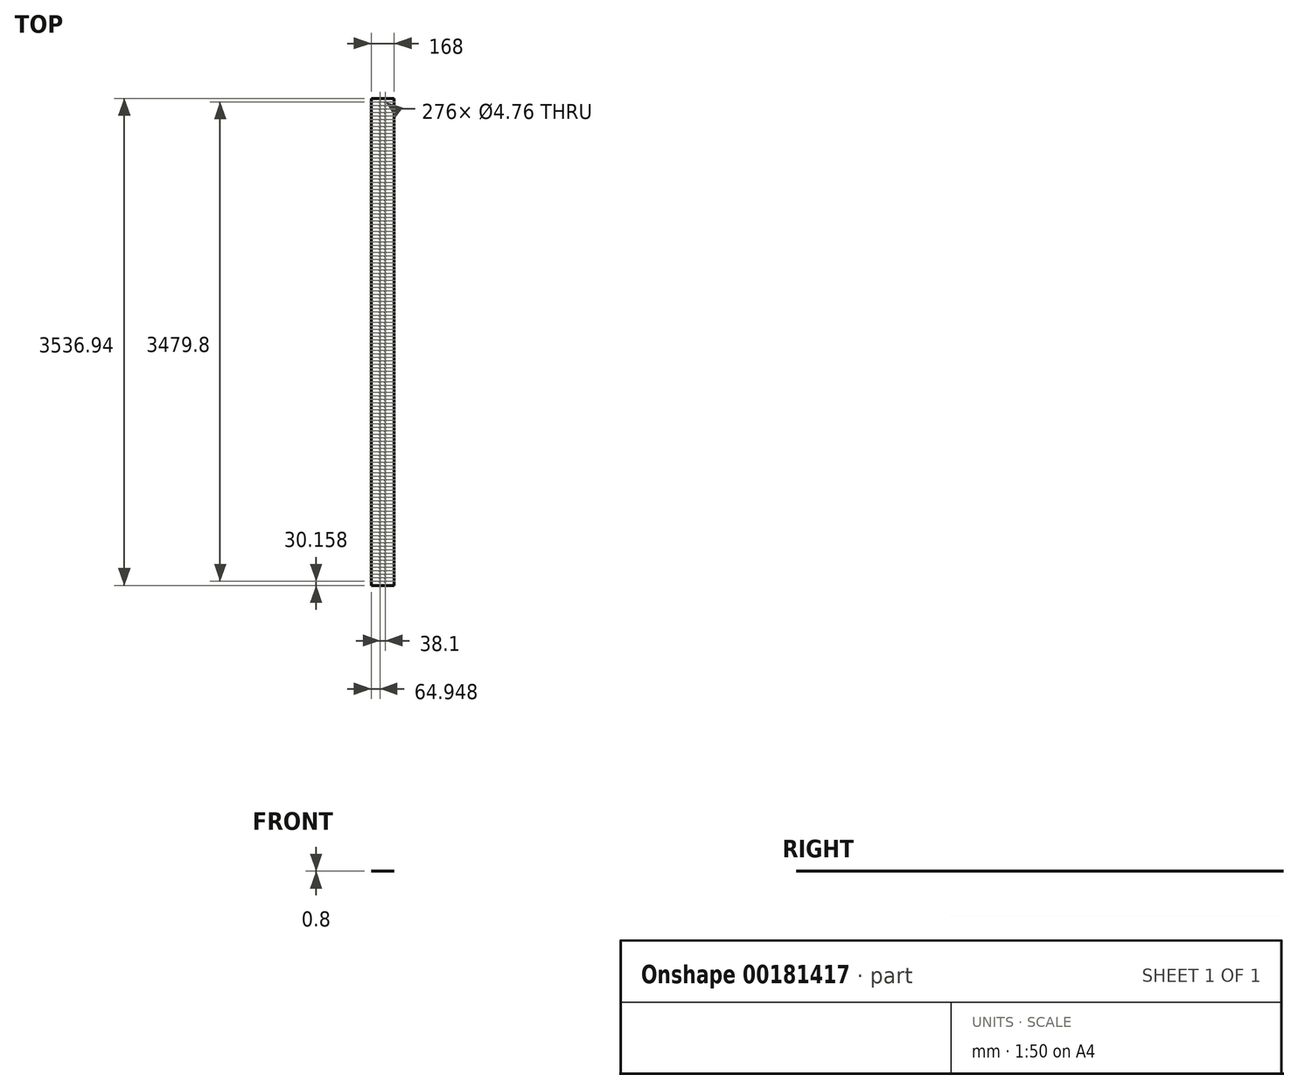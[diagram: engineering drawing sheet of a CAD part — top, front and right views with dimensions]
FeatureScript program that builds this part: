
annotation { "Feature Type Name" : "Feature", "Feature Type Description" : "" }
export const myFeature = defineFeature(function(context is Context, id is Id, definition is map)
    precondition{}
    {
        {
            var Q0;
            Q0=qCreatedBy(makeId("Top.planeOp"),FACE);
            var sketch = newSketch(context, id + "F0", { "sketchPlane" : qUnion([Q0])});
            skLineSegment(sketch, "E0.bottom", {"start": v(84, -1768.48) * mm, "end": v(-84, -1768.48) * mm});
            skLineSegment(sketch, "E0.top", {"start": v(84, 1768.48) * mm, "end": v(-84, 1768.48) * mm});
            skLineSegment(sketch, "E0.left", {"start": v(84, -1768.48) * mm, "end": v(84, 1768.48) * mm});
            skLineSegment(sketch, "E0.right", {"start": v(-84, -1768.48) * mm, "end": v(-84, 1768.48) * mm});
            skPoint(sketch, "E0.middle", {"position": v(0, 0) * mm});
            skCircle(sketch, "E1", {"center": v(-19.05, -1738.31) * mm, "radius": 2.38 * mm});
            skCircle(sketch, "E2.0.1.0", {"center": v(-19.05, -1712.91) * mm, "radius": 2.38 * mm});
            skCircle(sketch, "E2.0.2.0", {"center": v(-19.05, -1687.51) * mm, "radius": 2.38 * mm});
            skCircle(sketch, "E2.0.3.0", {"center": v(-19.05, -1662.11) * mm, "radius": 2.38 * mm});
            skCircle(sketch, "E2.0.4.0", {"center": v(-19.05, -1636.71) * mm, "radius": 2.38 * mm});
            skCircle(sketch, "E2.0.5.0", {"center": v(-19.05, -1611.31) * mm, "radius": 2.38 * mm});
            skCircle(sketch, "E2.0.6.0", {"center": v(-19.05, -1585.91) * mm, "radius": 2.38 * mm});
            skCircle(sketch, "E2.0.7.0", {"center": v(-19.05, -1560.51) * mm, "radius": 2.38 * mm});
            skCircle(sketch, "E2.0.8.0", {"center": v(-19.05, -1535.11) * mm, "radius": 2.38 * mm});
            skCircle(sketch, "E2.0.9.0", {"center": v(-19.05, -1509.71) * mm, "radius": 2.38 * mm});
            skCircle(sketch, "E2.0.10.0", {"center": v(-19.05, -1484.31) * mm, "radius": 2.38 * mm});
            skCircle(sketch, "E2.0.11.0", {"center": v(-19.05, -1458.91) * mm, "radius": 2.38 * mm});
            skCircle(sketch, "E2.0.12.0", {"center": v(-19.05, -1433.51) * mm, "radius": 2.38 * mm});
            skCircle(sketch, "E2.0.13.0", {"center": v(-19.05, -1408.11) * mm, "radius": 2.38 * mm});
            skCircle(sketch, "E2.0.14.0", {"center": v(-19.05, -1382.71) * mm, "radius": 2.38 * mm});
            skLineSegment(sketch, "E2.direction1", {"start": v(-19.05, -1738.31) * mm, "end": v(19.05, -1738.31) * mm, "construction": true});
            skLineSegment(sketch, "E2.direction2", {"start": v(-19.05, -1738.31) * mm, "end": v(-19.05, -1712.91) * mm, "construction": true});
            skCircle(sketch, "E3.0.1.0", {"center": v(19.05, -1738.31) * mm, "radius": 2.38 * mm});
            skCircle(sketch, "E3.0.1.1", {"center": v(19.05, -1712.91) * mm, "radius": 2.38 * mm});
            skCircle(sketch, "E3.0.1.2", {"center": v(19.05, -1687.51) * mm, "radius": 2.38 * mm});
            skCircle(sketch, "E3.0.1.3", {"center": v(19.05, -1662.11) * mm, "radius": 2.38 * mm});
            skCircle(sketch, "E3.0.1.4", {"center": v(19.05, -1636.71) * mm, "radius": 2.38 * mm});
            skCircle(sketch, "E3.0.1.5", {"center": v(19.05, -1611.31) * mm, "radius": 2.38 * mm});
            skCircle(sketch, "E3.0.1.6", {"center": v(19.05, -1585.91) * mm, "radius": 2.38 * mm});
            skCircle(sketch, "E3.0.1.7", {"center": v(19.05, -1560.51) * mm, "radius": 2.38 * mm});
            skCircle(sketch, "E3.0.1.8", {"center": v(19.05, -1535.11) * mm, "radius": 2.38 * mm});
            skCircle(sketch, "E3.0.1.9", {"center": v(19.05, -1509.71) * mm, "radius": 2.38 * mm});
            skCircle(sketch, "E3.0.1.10", {"center": v(19.05, -1484.31) * mm, "radius": 2.38 * mm});
            skCircle(sketch, "E3.0.1.11", {"center": v(19.05, -1458.91) * mm, "radius": 2.38 * mm});
            skCircle(sketch, "E3.0.1.12", {"center": v(19.05, -1433.51) * mm, "radius": 2.38 * mm});
            skCircle(sketch, "E3.0.1.13", {"center": v(19.05, -1408.11) * mm, "radius": 2.38 * mm});
            skCircle(sketch, "E3.0.1.14", {"center": v(19.05, -1382.71) * mm, "radius": 2.38 * mm});
            skCircle(sketch, "E4.0.0.15", {"center": v(-19.05, -1357.31) * mm, "radius": 2.38 * mm});
            skCircle(sketch, "E4.0.0.16", {"center": v(-19.05, -1331.91) * mm, "radius": 2.38 * mm});
            skCircle(sketch, "E4.0.0.17", {"center": v(-19.05, -1306.51) * mm, "radius": 2.38 * mm});
            skCircle(sketch, "E4.0.0.18", {"center": v(-19.05, -1281.11) * mm, "radius": 2.38 * mm});
            skCircle(sketch, "E4.0.0.19", {"center": v(-19.05, -1255.71) * mm, "radius": 2.38 * mm});
            skCircle(sketch, "E4.0.0.20", {"center": v(-19.05, -1230.31) * mm, "radius": 2.38 * mm});
            skCircle(sketch, "E4.0.0.21", {"center": v(-19.05, -1204.91) * mm, "radius": 2.38 * mm});
            skCircle(sketch, "E4.0.0.22", {"center": v(-19.05, -1179.51) * mm, "radius": 2.38 * mm});
            skCircle(sketch, "E4.0.0.23", {"center": v(-19.05, -1154.11) * mm, "radius": 2.38 * mm});
            skCircle(sketch, "E4.0.0.24", {"center": v(-19.05, -1128.71) * mm, "radius": 2.38 * mm});
            skCircle(sketch, "E4.0.0.25", {"center": v(-19.05, -1103.31) * mm, "radius": 2.38 * mm});
            skCircle(sketch, "E4.0.0.26", {"center": v(-19.05, -1077.91) * mm, "radius": 2.38 * mm});
            skCircle(sketch, "E4.0.0.27", {"center": v(-19.05, -1052.51) * mm, "radius": 2.38 * mm});
            skCircle(sketch, "E4.0.0.28", {"center": v(-19.05, -1027.11) * mm, "radius": 2.38 * mm});
            skCircle(sketch, "E4.0.0.29", {"center": v(-19.05, -1001.71) * mm, "radius": 2.38 * mm});
            skCircle(sketch, "E4.0.1.15", {"center": v(19.05, -1357.31) * mm, "radius": 2.38 * mm});
            skCircle(sketch, "E4.0.1.16", {"center": v(19.05, -1331.91) * mm, "radius": 2.38 * mm});
            skCircle(sketch, "E4.0.1.17", {"center": v(19.05, -1306.51) * mm, "radius": 2.38 * mm});
            skCircle(sketch, "E4.0.1.18", {"center": v(19.05, -1281.11) * mm, "radius": 2.38 * mm});
            skCircle(sketch, "E4.0.1.19", {"center": v(19.05, -1255.71) * mm, "radius": 2.38 * mm});
            skCircle(sketch, "E4.0.1.20", {"center": v(19.05, -1230.31) * mm, "radius": 2.38 * mm});
            skCircle(sketch, "E4.0.1.21", {"center": v(19.05, -1204.91) * mm, "radius": 2.38 * mm});
            skCircle(sketch, "E4.0.1.22", {"center": v(19.05, -1179.51) * mm, "radius": 2.38 * mm});
            skCircle(sketch, "E4.0.1.23", {"center": v(19.05, -1154.11) * mm, "radius": 2.38 * mm});
            skCircle(sketch, "E4.0.1.24", {"center": v(19.05, -1128.71) * mm, "radius": 2.38 * mm});
            skCircle(sketch, "E4.0.1.25", {"center": v(19.05, -1103.31) * mm, "radius": 2.38 * mm});
            skCircle(sketch, "E4.0.1.26", {"center": v(19.05, -1077.91) * mm, "radius": 2.38 * mm});
            skCircle(sketch, "E4.0.1.27", {"center": v(19.05, -1052.51) * mm, "radius": 2.38 * mm});
            skCircle(sketch, "E4.0.1.28", {"center": v(19.05, -1027.11) * mm, "radius": 2.38 * mm});
            skCircle(sketch, "E4.0.1.29", {"center": v(19.05, -1001.71) * mm, "radius": 2.38 * mm});
            skCircle(sketch, "E5.0.0.30", {"center": v(-19.05, -976.31) * mm, "radius": 2.38 * mm});
            skCircle(sketch, "E5.0.0.31", {"center": v(-19.05, -950.91) * mm, "radius": 2.38 * mm});
            skCircle(sketch, "E5.0.0.32", {"center": v(-19.05, -925.51) * mm, "radius": 2.38 * mm});
            skCircle(sketch, "E5.0.0.33", {"center": v(-19.05, -900.11) * mm, "radius": 2.38 * mm});
            skCircle(sketch, "E5.0.0.34", {"center": v(-19.05, -874.71) * mm, "radius": 2.38 * mm});
            skCircle(sketch, "E5.0.0.35", {"center": v(-19.05, -849.31) * mm, "radius": 2.38 * mm});
            skCircle(sketch, "E5.0.0.36", {"center": v(-19.05, -823.91) * mm, "radius": 2.38 * mm});
            skCircle(sketch, "E5.0.0.37", {"center": v(-19.05, -798.51) * mm, "radius": 2.38 * mm});
            skCircle(sketch, "E5.0.0.38", {"center": v(-19.05, -773.11) * mm, "radius": 2.38 * mm});
            skCircle(sketch, "E5.0.0.39", {"center": v(-19.05, -747.71) * mm, "radius": 2.38 * mm});
            skCircle(sketch, "E5.0.0.40", {"center": v(-19.05, -722.31) * mm, "radius": 2.38 * mm});
            skCircle(sketch, "E5.0.0.41", {"center": v(-19.05, -696.91) * mm, "radius": 2.38 * mm});
            skCircle(sketch, "E5.0.0.42", {"center": v(-19.05, -671.51) * mm, "radius": 2.38 * mm});
            skCircle(sketch, "E5.0.0.43", {"center": v(-19.05, -646.11) * mm, "radius": 2.38 * mm});
            skCircle(sketch, "E5.0.0.44", {"center": v(-19.05, -620.71) * mm, "radius": 2.38 * mm});
            skCircle(sketch, "E5.0.0.45", {"center": v(-19.05, -595.31) * mm, "radius": 2.38 * mm});
            skCircle(sketch, "E5.0.0.46", {"center": v(-19.05, -569.91) * mm, "radius": 2.38 * mm});
            skCircle(sketch, "E5.0.0.47", {"center": v(-19.05, -544.51) * mm, "radius": 2.38 * mm});
            skCircle(sketch, "E5.0.0.48", {"center": v(-19.05, -519.11) * mm, "radius": 2.38 * mm});
            skCircle(sketch, "E5.0.0.49", {"center": v(-19.05, -493.71) * mm, "radius": 2.38 * mm});
            skCircle(sketch, "E5.0.0.50", {"center": v(-19.05, -468.31) * mm, "radius": 2.38 * mm});
            skCircle(sketch, "E5.0.0.51", {"center": v(-19.05, -442.91) * mm, "radius": 2.38 * mm});
            skCircle(sketch, "E5.0.0.52", {"center": v(-19.05, -417.51) * mm, "radius": 2.38 * mm});
            skCircle(sketch, "E5.0.0.53", {"center": v(-19.05, -392.11) * mm, "radius": 2.38 * mm});
            skCircle(sketch, "E5.0.0.54", {"center": v(-19.05, -366.71) * mm, "radius": 2.38 * mm});
            skCircle(sketch, "E5.0.0.55", {"center": v(-19.05, -341.31) * mm, "radius": 2.38 * mm});
            skCircle(sketch, "E5.0.0.56", {"center": v(-19.05, -315.91) * mm, "radius": 2.38 * mm});
            skCircle(sketch, "E5.0.0.57", {"center": v(-19.05, -290.51) * mm, "radius": 2.38 * mm});
            skCircle(sketch, "E5.0.0.58", {"center": v(-19.05, -265.11) * mm, "radius": 2.38 * mm});
            skCircle(sketch, "E5.0.0.59", {"center": v(-19.05, -239.71) * mm, "radius": 2.38 * mm});
            skCircle(sketch, "E5.0.0.60", {"center": v(-19.05, -214.31) * mm, "radius": 2.38 * mm});
            skCircle(sketch, "E5.0.0.61", {"center": v(-19.05, -188.91) * mm, "radius": 2.38 * mm});
            skCircle(sketch, "E5.0.0.62", {"center": v(-19.05, -163.51) * mm, "radius": 2.38 * mm});
            skCircle(sketch, "E5.0.0.63", {"center": v(-19.05, -138.11) * mm, "radius": 2.38 * mm});
            skCircle(sketch, "E5.0.0.64", {"center": v(-19.05, -112.71) * mm, "radius": 2.38 * mm});
            skCircle(sketch, "E5.0.0.65", {"center": v(-19.05, -87.31) * mm, "radius": 2.38 * mm});
            skCircle(sketch, "E5.0.0.66", {"center": v(-19.05, -61.91) * mm, "radius": 2.38 * mm});
            skCircle(sketch, "E5.0.0.67", {"center": v(-19.05, -36.51) * mm, "radius": 2.38 * mm});
            skCircle(sketch, "E5.0.0.68", {"center": v(-19.05, -11.11) * mm, "radius": 2.38 * mm});
            skCircle(sketch, "E5.0.0.69", {"center": v(-19.05, 14.29) * mm, "radius": 2.38 * mm});
            skCircle(sketch, "E5.0.0.70", {"center": v(-19.05, 39.69) * mm, "radius": 2.38 * mm});
            skCircle(sketch, "E5.0.0.71", {"center": v(-19.05, 65.09) * mm, "radius": 2.38 * mm});
            skCircle(sketch, "E5.0.0.72", {"center": v(-19.05, 90.49) * mm, "radius": 2.38 * mm});
            skCircle(sketch, "E5.0.0.73", {"center": v(-19.05, 115.89) * mm, "radius": 2.38 * mm});
            skCircle(sketch, "E5.0.0.74", {"center": v(-19.05, 141.29) * mm, "radius": 2.38 * mm});
            skCircle(sketch, "E5.0.0.75", {"center": v(-19.05, 166.69) * mm, "radius": 2.38 * mm});
            skCircle(sketch, "E5.0.0.76", {"center": v(-19.05, 192.09) * mm, "radius": 2.38 * mm});
            skCircle(sketch, "E5.0.0.77", {"center": v(-19.05, 217.49) * mm, "radius": 2.38 * mm});
            skCircle(sketch, "E5.0.0.78", {"center": v(-19.05, 242.89) * mm, "radius": 2.38 * mm});
            skCircle(sketch, "E5.0.0.79", {"center": v(-19.05, 268.29) * mm, "radius": 2.38 * mm});
            skCircle(sketch, "E5.0.0.80", {"center": v(-19.05, 293.69) * mm, "radius": 2.38 * mm});
            skCircle(sketch, "E5.0.0.81", {"center": v(-19.05, 319.09) * mm, "radius": 2.38 * mm});
            skCircle(sketch, "E5.0.0.82", {"center": v(-19.05, 344.49) * mm, "radius": 2.38 * mm});
            skCircle(sketch, "E5.0.0.83", {"center": v(-19.05, 369.89) * mm, "radius": 2.38 * mm});
            skCircle(sketch, "E5.0.0.84", {"center": v(-19.05, 395.29) * mm, "radius": 2.38 * mm});
            skCircle(sketch, "E5.0.0.85", {"center": v(-19.05, 420.69) * mm, "radius": 2.38 * mm});
            skCircle(sketch, "E5.0.0.86", {"center": v(-19.05, 446.09) * mm, "radius": 2.38 * mm});
            skCircle(sketch, "E5.0.0.87", {"center": v(-19.05, 471.49) * mm, "radius": 2.38 * mm});
            skCircle(sketch, "E5.0.0.88", {"center": v(-19.05, 496.89) * mm, "radius": 2.38 * mm});
            skCircle(sketch, "E5.0.0.89", {"center": v(-19.05, 522.29) * mm, "radius": 2.38 * mm});
            skCircle(sketch, "E5.0.0.90", {"center": v(-19.05, 547.69) * mm, "radius": 2.38 * mm});
            skCircle(sketch, "E5.0.0.91", {"center": v(-19.05, 573.09) * mm, "radius": 2.38 * mm});
            skCircle(sketch, "E5.0.0.92", {"center": v(-19.05, 598.49) * mm, "radius": 2.38 * mm});
            skCircle(sketch, "E5.0.0.93", {"center": v(-19.05, 623.89) * mm, "radius": 2.38 * mm});
            skCircle(sketch, "E5.0.0.94", {"center": v(-19.05, 649.29) * mm, "radius": 2.38 * mm});
            skCircle(sketch, "E5.0.0.95", {"center": v(-19.05, 674.69) * mm, "radius": 2.38 * mm});
            skCircle(sketch, "E5.0.0.96", {"center": v(-19.05, 700.09) * mm, "radius": 2.38 * mm});
            skCircle(sketch, "E5.0.0.97", {"center": v(-19.05, 725.49) * mm, "radius": 2.38 * mm});
            skCircle(sketch, "E5.0.0.98", {"center": v(-19.05, 750.89) * mm, "radius": 2.38 * mm});
            skCircle(sketch, "E5.0.0.99", {"center": v(-19.05, 776.29) * mm, "radius": 2.38 * mm});
            skCircle(sketch, "E5.0.1.30", {"center": v(19.05, -976.31) * mm, "radius": 2.38 * mm});
            skCircle(sketch, "E5.0.1.31", {"center": v(19.05, -950.91) * mm, "radius": 2.38 * mm});
            skCircle(sketch, "E5.0.1.32", {"center": v(19.05, -925.51) * mm, "radius": 2.38 * mm});
            skCircle(sketch, "E5.0.1.33", {"center": v(19.05, -900.11) * mm, "radius": 2.38 * mm});
            skCircle(sketch, "E5.0.1.34", {"center": v(19.05, -874.71) * mm, "radius": 2.38 * mm});
            skCircle(sketch, "E5.0.1.35", {"center": v(19.05, -849.31) * mm, "radius": 2.38 * mm});
            skCircle(sketch, "E5.0.1.36", {"center": v(19.05, -823.91) * mm, "radius": 2.38 * mm});
            skCircle(sketch, "E5.0.1.37", {"center": v(19.05, -798.51) * mm, "radius": 2.38 * mm});
            skCircle(sketch, "E5.0.1.38", {"center": v(19.05, -773.11) * mm, "radius": 2.38 * mm});
            skCircle(sketch, "E5.0.1.39", {"center": v(19.05, -747.71) * mm, "radius": 2.38 * mm});
            skCircle(sketch, "E5.0.1.40", {"center": v(19.05, -722.31) * mm, "radius": 2.38 * mm});
            skCircle(sketch, "E5.0.1.41", {"center": v(19.05, -696.91) * mm, "radius": 2.38 * mm});
            skCircle(sketch, "E5.0.1.42", {"center": v(19.05, -671.51) * mm, "radius": 2.38 * mm});
            skCircle(sketch, "E5.0.1.43", {"center": v(19.05, -646.11) * mm, "radius": 2.38 * mm});
            skCircle(sketch, "E5.0.1.44", {"center": v(19.05, -620.71) * mm, "radius": 2.38 * mm});
            skCircle(sketch, "E5.0.1.45", {"center": v(19.05, -595.31) * mm, "radius": 2.38 * mm});
            skCircle(sketch, "E5.0.1.46", {"center": v(19.05, -569.91) * mm, "radius": 2.38 * mm});
            skCircle(sketch, "E5.0.1.47", {"center": v(19.05, -544.51) * mm, "radius": 2.38 * mm});
            skCircle(sketch, "E5.0.1.48", {"center": v(19.05, -519.11) * mm, "radius": 2.38 * mm});
            skCircle(sketch, "E5.0.1.49", {"center": v(19.05, -493.71) * mm, "radius": 2.38 * mm});
            skCircle(sketch, "E5.0.1.50", {"center": v(19.05, -468.31) * mm, "radius": 2.38 * mm});
            skCircle(sketch, "E5.0.1.51", {"center": v(19.05, -442.91) * mm, "radius": 2.38 * mm});
            skCircle(sketch, "E5.0.1.52", {"center": v(19.05, -417.51) * mm, "radius": 2.38 * mm});
            skCircle(sketch, "E5.0.1.53", {"center": v(19.05, -392.11) * mm, "radius": 2.38 * mm});
            skCircle(sketch, "E5.0.1.54", {"center": v(19.05, -366.71) * mm, "radius": 2.38 * mm});
            skCircle(sketch, "E5.0.1.55", {"center": v(19.05, -341.31) * mm, "radius": 2.38 * mm});
            skCircle(sketch, "E5.0.1.56", {"center": v(19.05, -315.91) * mm, "radius": 2.38 * mm});
            skCircle(sketch, "E5.0.1.57", {"center": v(19.05, -290.51) * mm, "radius": 2.38 * mm});
            skCircle(sketch, "E5.0.1.58", {"center": v(19.05, -265.11) * mm, "radius": 2.38 * mm});
            skCircle(sketch, "E5.0.1.59", {"center": v(19.05, -239.71) * mm, "radius": 2.38 * mm});
            skCircle(sketch, "E5.0.1.60", {"center": v(19.05, -214.31) * mm, "radius": 2.38 * mm});
            skCircle(sketch, "E5.0.1.61", {"center": v(19.05, -188.91) * mm, "radius": 2.38 * mm});
            skCircle(sketch, "E5.0.1.62", {"center": v(19.05, -163.51) * mm, "radius": 2.38 * mm});
            skCircle(sketch, "E5.0.1.63", {"center": v(19.05, -138.11) * mm, "radius": 2.38 * mm});
            skCircle(sketch, "E5.0.1.64", {"center": v(19.05, -112.71) * mm, "radius": 2.38 * mm});
            skCircle(sketch, "E5.0.1.65", {"center": v(19.05, -87.31) * mm, "radius": 2.38 * mm});
            skCircle(sketch, "E5.0.1.66", {"center": v(19.05, -61.91) * mm, "radius": 2.38 * mm});
            skCircle(sketch, "E5.0.1.67", {"center": v(19.05, -36.51) * mm, "radius": 2.38 * mm});
            skCircle(sketch, "E5.0.1.68", {"center": v(19.05, -11.11) * mm, "radius": 2.38 * mm});
            skCircle(sketch, "E5.0.1.69", {"center": v(19.05, 14.29) * mm, "radius": 2.38 * mm});
            skCircle(sketch, "E5.0.1.70", {"center": v(19.05, 39.69) * mm, "radius": 2.38 * mm});
            skCircle(sketch, "E5.0.1.71", {"center": v(19.05, 65.09) * mm, "radius": 2.38 * mm});
            skCircle(sketch, "E5.0.1.72", {"center": v(19.05, 90.49) * mm, "radius": 2.38 * mm});
            skCircle(sketch, "E5.0.1.73", {"center": v(19.05, 115.89) * mm, "radius": 2.38 * mm});
            skCircle(sketch, "E5.0.1.74", {"center": v(19.05, 141.29) * mm, "radius": 2.38 * mm});
            skCircle(sketch, "E5.0.1.75", {"center": v(19.05, 166.69) * mm, "radius": 2.38 * mm});
            skCircle(sketch, "E5.0.1.76", {"center": v(19.05, 192.09) * mm, "radius": 2.38 * mm});
            skCircle(sketch, "E5.0.1.77", {"center": v(19.05, 217.49) * mm, "radius": 2.38 * mm});
            skCircle(sketch, "E5.0.1.78", {"center": v(19.05, 242.89) * mm, "radius": 2.38 * mm});
            skCircle(sketch, "E5.0.1.79", {"center": v(19.05, 268.29) * mm, "radius": 2.38 * mm});
            skCircle(sketch, "E5.0.1.80", {"center": v(19.05, 293.69) * mm, "radius": 2.38 * mm});
            skCircle(sketch, "E5.0.1.81", {"center": v(19.05, 319.09) * mm, "radius": 2.38 * mm});
            skCircle(sketch, "E5.0.1.82", {"center": v(19.05, 344.49) * mm, "radius": 2.38 * mm});
            skCircle(sketch, "E5.0.1.83", {"center": v(19.05, 369.89) * mm, "radius": 2.38 * mm});
            skCircle(sketch, "E5.0.1.84", {"center": v(19.05, 395.29) * mm, "radius": 2.38 * mm});
            skCircle(sketch, "E5.0.1.85", {"center": v(19.05, 420.69) * mm, "radius": 2.38 * mm});
            skCircle(sketch, "E5.0.1.86", {"center": v(19.05, 446.09) * mm, "radius": 2.38 * mm});
            skCircle(sketch, "E5.0.1.87", {"center": v(19.05, 471.49) * mm, "radius": 2.38 * mm});
            skCircle(sketch, "E5.0.1.88", {"center": v(19.05, 496.89) * mm, "radius": 2.38 * mm});
            skCircle(sketch, "E5.0.1.89", {"center": v(19.05, 522.29) * mm, "radius": 2.38 * mm});
            skCircle(sketch, "E5.0.1.90", {"center": v(19.05, 547.69) * mm, "radius": 2.38 * mm});
            skCircle(sketch, "E5.0.1.91", {"center": v(19.05, 573.09) * mm, "radius": 2.38 * mm});
            skCircle(sketch, "E5.0.1.92", {"center": v(19.05, 598.49) * mm, "radius": 2.38 * mm});
            skCircle(sketch, "E5.0.1.93", {"center": v(19.05, 623.89) * mm, "radius": 2.38 * mm});
            skCircle(sketch, "E5.0.1.94", {"center": v(19.05, 649.29) * mm, "radius": 2.38 * mm});
            skCircle(sketch, "E5.0.1.95", {"center": v(19.05, 674.69) * mm, "radius": 2.38 * mm});
            skCircle(sketch, "E5.0.1.96", {"center": v(19.05, 700.09) * mm, "radius": 2.38 * mm});
            skCircle(sketch, "E5.0.1.97", {"center": v(19.05, 725.49) * mm, "radius": 2.38 * mm});
            skCircle(sketch, "E5.0.1.98", {"center": v(19.05, 750.89) * mm, "radius": 2.38 * mm});
            skCircle(sketch, "E5.0.1.99", {"center": v(19.05, 776.29) * mm, "radius": 2.38 * mm});
            skCircle(sketch, "E6.0.1.0", {"center": v(-19.05, 801.69) * mm, "radius": 2.38 * mm});
            skCircle(sketch, "E6.0.2.0", {"center": v(-19.05, 827.09) * mm, "radius": 2.38 * mm});
            skCircle(sketch, "E6.0.3.0", {"center": v(-19.05, 852.49) * mm, "radius": 2.38 * mm});
            skCircle(sketch, "E6.0.4.0", {"center": v(-19.05, 877.89) * mm, "radius": 2.38 * mm});
            skCircle(sketch, "E6.0.5.0", {"center": v(-19.05, 903.29) * mm, "radius": 2.38 * mm});
            skCircle(sketch, "E6.0.6.0", {"center": v(-19.05, 928.69) * mm, "radius": 2.38 * mm});
            skCircle(sketch, "E6.0.7.0", {"center": v(-19.05, 954.09) * mm, "radius": 2.38 * mm});
            skCircle(sketch, "E6.0.8.0", {"center": v(-19.05, 979.49) * mm, "radius": 2.38 * mm});
            skCircle(sketch, "E6.0.9.0", {"center": v(-19.05, 1004.89) * mm, "radius": 2.38 * mm});
            skCircle(sketch, "E6.0.10.0", {"center": v(-19.05, 1030.29) * mm, "radius": 2.38 * mm});
            skCircle(sketch, "E6.0.11.0", {"center": v(-19.05, 1055.69) * mm, "radius": 2.38 * mm});
            skCircle(sketch, "E6.0.12.0", {"center": v(-19.05, 1081.09) * mm, "radius": 2.38 * mm});
            skCircle(sketch, "E6.0.13.0", {"center": v(-19.05, 1106.49) * mm, "radius": 2.38 * mm});
            skCircle(sketch, "E6.0.14.0", {"center": v(-19.05, 1131.89) * mm, "radius": 2.38 * mm});
            skCircle(sketch, "E6.0.15.0", {"center": v(-19.05, 1157.29) * mm, "radius": 2.38 * mm});
            skCircle(sketch, "E6.0.16.0", {"center": v(-19.05, 1182.69) * mm, "radius": 2.38 * mm});
            skCircle(sketch, "E6.0.17.0", {"center": v(-19.05, 1208.09) * mm, "radius": 2.38 * mm});
            skCircle(sketch, "E6.0.18.0", {"center": v(-19.05, 1233.49) * mm, "radius": 2.38 * mm});
            skCircle(sketch, "E6.0.19.0", {"center": v(-19.05, 1258.89) * mm, "radius": 2.38 * mm});
            skCircle(sketch, "E6.0.20.0", {"center": v(-19.05, 1284.29) * mm, "radius": 2.38 * mm});
            skCircle(sketch, "E6.0.21.0", {"center": v(-19.05, 1309.69) * mm, "radius": 2.38 * mm});
            skCircle(sketch, "E6.0.22.0", {"center": v(-19.05, 1335.09) * mm, "radius": 2.38 * mm});
            skCircle(sketch, "E6.0.23.0", {"center": v(-19.05, 1360.49) * mm, "radius": 2.38 * mm});
            skCircle(sketch, "E6.0.24.0", {"center": v(-19.05, 1385.89) * mm, "radius": 2.38 * mm});
            skCircle(sketch, "E6.0.25.0", {"center": v(-19.05, 1411.29) * mm, "radius": 2.38 * mm});
            skCircle(sketch, "E6.0.26.0", {"center": v(-19.05, 1436.69) * mm, "radius": 2.38 * mm});
            skCircle(sketch, "E6.0.27.0", {"center": v(-19.05, 1462.09) * mm, "radius": 2.38 * mm});
            skCircle(sketch, "E6.0.28.0", {"center": v(-19.05, 1487.49) * mm, "radius": 2.38 * mm});
            skCircle(sketch, "E6.0.29.0", {"center": v(-19.05, 1512.89) * mm, "radius": 2.38 * mm});
            skCircle(sketch, "E6.1.1.0", {"center": v(19.05, 801.69) * mm, "radius": 2.38 * mm});
            skCircle(sketch, "E6.1.2.0", {"center": v(19.05, 827.09) * mm, "radius": 2.38 * mm});
            skCircle(sketch, "E6.1.3.0", {"center": v(19.05, 852.49) * mm, "radius": 2.38 * mm});
            skCircle(sketch, "E6.1.4.0", {"center": v(19.05, 877.89) * mm, "radius": 2.38 * mm});
            skCircle(sketch, "E6.1.5.0", {"center": v(19.05, 903.29) * mm, "radius": 2.38 * mm});
            skCircle(sketch, "E6.1.6.0", {"center": v(19.05, 928.69) * mm, "radius": 2.38 * mm});
            skCircle(sketch, "E6.1.7.0", {"center": v(19.05, 954.09) * mm, "radius": 2.38 * mm});
            skCircle(sketch, "E6.1.8.0", {"center": v(19.05, 979.49) * mm, "radius": 2.38 * mm});
            skCircle(sketch, "E6.1.9.0", {"center": v(19.05, 1004.89) * mm, "radius": 2.38 * mm});
            skCircle(sketch, "E6.1.10.0", {"center": v(19.05, 1030.29) * mm, "radius": 2.38 * mm});
            skCircle(sketch, "E6.1.11.0", {"center": v(19.05, 1055.69) * mm, "radius": 2.38 * mm});
            skCircle(sketch, "E6.1.12.0", {"center": v(19.05, 1081.09) * mm, "radius": 2.38 * mm});
            skCircle(sketch, "E6.1.13.0", {"center": v(19.05, 1106.49) * mm, "radius": 2.38 * mm});
            skCircle(sketch, "E6.1.14.0", {"center": v(19.05, 1131.89) * mm, "radius": 2.38 * mm});
            skCircle(sketch, "E6.1.15.0", {"center": v(19.05, 1157.29) * mm, "radius": 2.38 * mm});
            skCircle(sketch, "E6.1.16.0", {"center": v(19.05, 1182.69) * mm, "radius": 2.38 * mm});
            skCircle(sketch, "E6.1.17.0", {"center": v(19.05, 1208.09) * mm, "radius": 2.38 * mm});
            skCircle(sketch, "E6.1.18.0", {"center": v(19.05, 1233.49) * mm, "radius": 2.38 * mm});
            skCircle(sketch, "E6.1.19.0", {"center": v(19.05, 1258.89) * mm, "radius": 2.38 * mm});
            skCircle(sketch, "E6.1.20.0", {"center": v(19.05, 1284.29) * mm, "radius": 2.38 * mm});
            skCircle(sketch, "E6.1.21.0", {"center": v(19.05, 1309.69) * mm, "radius": 2.38 * mm});
            skCircle(sketch, "E6.1.22.0", {"center": v(19.05, 1335.09) * mm, "radius": 2.38 * mm});
            skCircle(sketch, "E6.1.23.0", {"center": v(19.05, 1360.49) * mm, "radius": 2.38 * mm});
            skCircle(sketch, "E6.1.24.0", {"center": v(19.05, 1385.89) * mm, "radius": 2.38 * mm});
            skCircle(sketch, "E6.1.25.0", {"center": v(19.05, 1411.29) * mm, "radius": 2.38 * mm});
            skCircle(sketch, "E6.1.26.0", {"center": v(19.05, 1436.69) * mm, "radius": 2.38 * mm});
            skCircle(sketch, "E6.1.27.0", {"center": v(19.05, 1462.09) * mm, "radius": 2.38 * mm});
            skCircle(sketch, "E6.1.28.0", {"center": v(19.05, 1487.49) * mm, "radius": 2.38 * mm});
            skCircle(sketch, "E6.1.29.0", {"center": v(19.05, 1512.89) * mm, "radius": 2.38 * mm});
            skLineSegment(sketch, "E6.direction1", {"start": v(-19.05, 776.29) * mm, "end": v(19.05, 776.29) * mm, "construction": true});
            skLineSegment(sketch, "E6.direction2", {"start": v(-19.05, 776.29) * mm, "end": v(-19.05, 801.69) * mm, "construction": true});
            skCircle(sketch, "E7.0.0.30", {"center": v(-19.05, 1538.29) * mm, "radius": 2.38 * mm});
            skCircle(sketch, "E7.0.0.31", {"center": v(-19.05, 1563.69) * mm, "radius": 2.38 * mm});
            skCircle(sketch, "E7.0.0.32", {"center": v(-19.05, 1589.09) * mm, "radius": 2.38 * mm});
            skCircle(sketch, "E7.0.0.33", {"center": v(-19.05, 1614.49) * mm, "radius": 2.38 * mm});
            skCircle(sketch, "E7.0.0.34", {"center": v(-19.05, 1639.89) * mm, "radius": 2.38 * mm});
            skCircle(sketch, "E7.0.0.35", {"center": v(-19.05, 1665.29) * mm, "radius": 2.38 * mm});
            skCircle(sketch, "E7.0.0.36", {"center": v(-19.05, 1690.69) * mm, "radius": 2.38 * mm});
            skCircle(sketch, "E7.0.0.37", {"center": v(-19.05, 1716.09) * mm, "radius": 2.38 * mm});
            skCircle(sketch, "E7.0.0.38", {"center": v(-19.05, 1741.49) * mm, "radius": 2.38 * mm});
            skCircle(sketch, "E7.0.1.30", {"center": v(19.05, 1538.29) * mm, "radius": 2.38 * mm});
            skCircle(sketch, "E7.0.1.31", {"center": v(19.05, 1563.69) * mm, "radius": 2.38 * mm});
            skCircle(sketch, "E7.0.1.32", {"center": v(19.05, 1589.09) * mm, "radius": 2.38 * mm});
            skCircle(sketch, "E7.0.1.33", {"center": v(19.05, 1614.49) * mm, "radius": 2.38 * mm});
            skCircle(sketch, "E7.0.1.34", {"center": v(19.05, 1639.89) * mm, "radius": 2.38 * mm});
            skCircle(sketch, "E7.0.1.35", {"center": v(19.05, 1665.29) * mm, "radius": 2.38 * mm});
            skCircle(sketch, "E7.0.1.36", {"center": v(19.05, 1690.69) * mm, "radius": 2.38 * mm});
            skCircle(sketch, "E7.0.1.37", {"center": v(19.05, 1716.09) * mm, "radius": 2.38 * mm});
            skCircle(sketch, "E7.0.1.38", {"center": v(19.05, 1741.49) * mm, "radius": 2.38 * mm});
            skSolve(sketch);
        }
        {
            var Q0;
            {var subQ1=sQuery(id+"F0.wireOp",EDGE,"E0.left");Q0=makeQuery(id+"F0.imprint","IMPRINT",FACE,{"disambiguationData":[TD([[makeQuery(id+"F0.imprint","IMPRINT",EDGE,{"derivedFrom":subQ1}),1.0]])]});}
            var Q1;
            {var subQ0=sQuery(id+"F0.wireOp",EDGE,"E0.right");Q1=makeQuery(id+"F0.imprint","IMPRINT",FACE,{"disambiguationData":[TD([[makeQuery(id+"F0.imprint","IMPRINT",EDGE,{"derivedFrom":subQ0}),-1.0]])]});}
            extrude(context, id + "F1", {"entities" : qUnion([Q0, Q1]), "depth" : .8 * mm});
        }
    });
